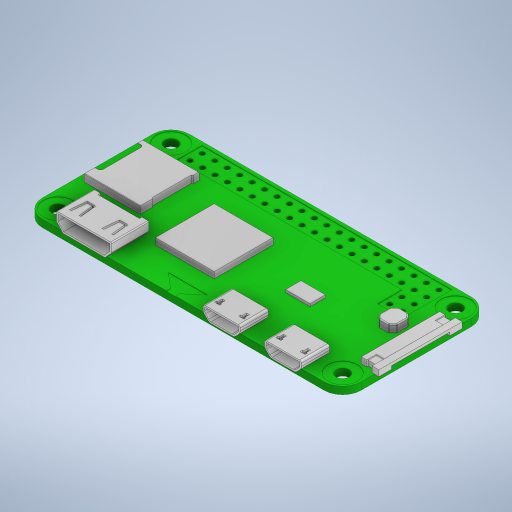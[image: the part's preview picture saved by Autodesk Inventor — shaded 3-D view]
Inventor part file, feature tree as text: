
AUTODESK INVENTOR PART (.ipt)
format: ipt  version: 2023 (Build 270158000, 158)  size: 594,432 bytes
history: imported  units: in
note: dims shown in document units (in); Inventor stores cm internally (conversion verified against a paired STEP export)
features: plane x1, split x1, imported_body x1
ambient origin geometry x8: Origin, YZ Plane, XZ Plane, XY Plane, X Axis, Y Axis, Z Axis, Center Point
bodies: Solid1 (imported_parasolid), Solid2 (imported_parasolid), Body1 (imported_parasolid), Body2 (imported_parasolid), Solid3 (imported_parasolid), Solid4 (imported_parasolid)
feature tree (3):
  plane  "Work Plane1"
  split  "Split1"
  imported_body  NMx_Import_Brep_tag  [imported B-rep: ~317 faces, bbox_mm=[65.9, 4.8, 31.25]]
